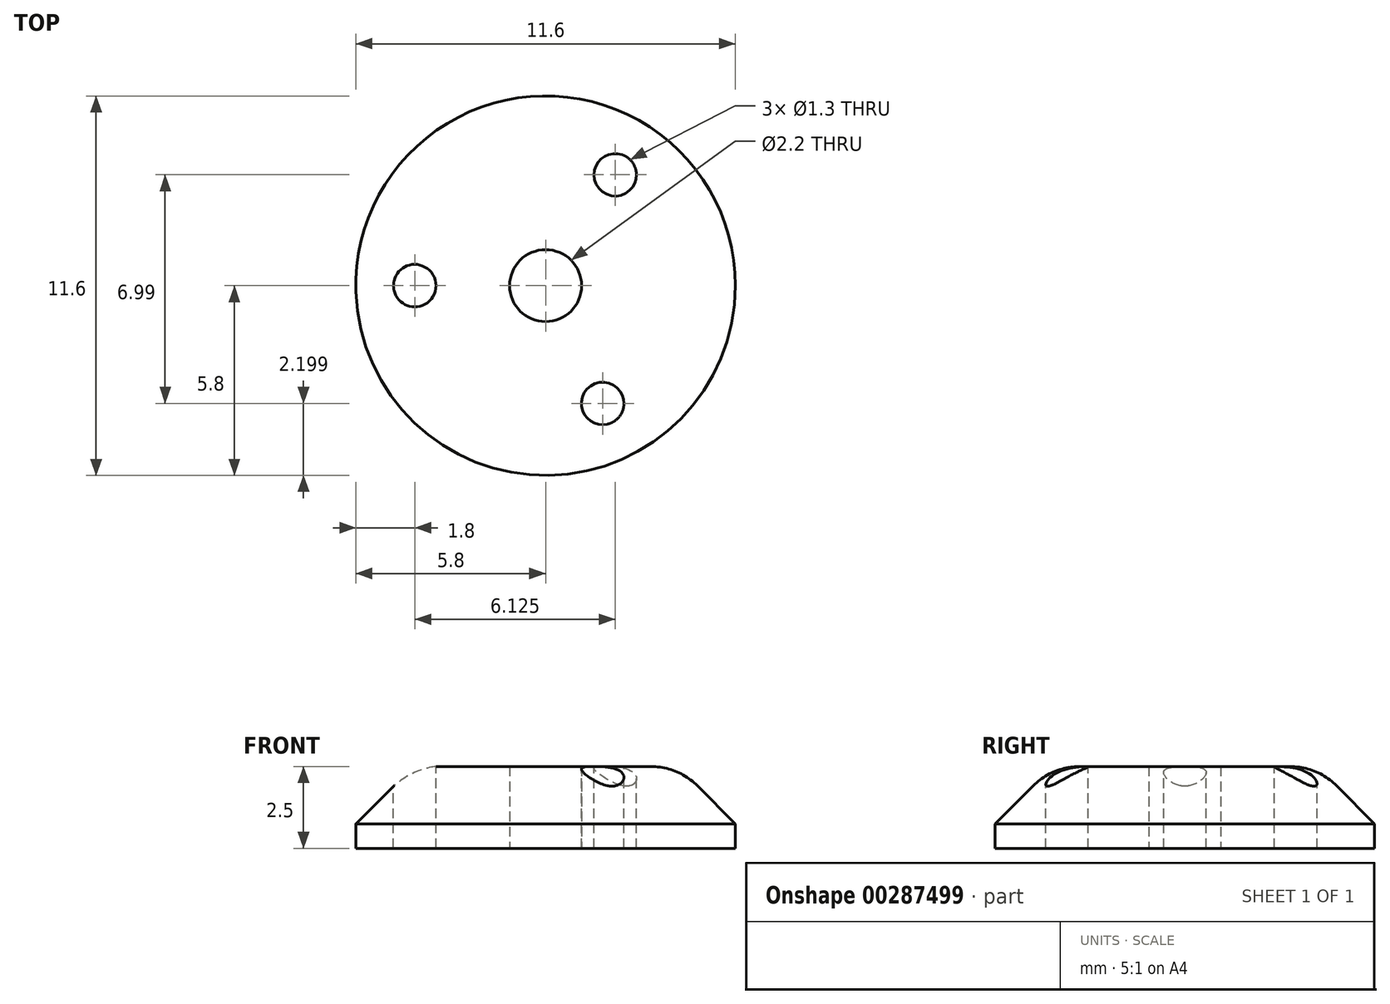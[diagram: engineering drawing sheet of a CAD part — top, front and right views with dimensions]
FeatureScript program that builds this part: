
annotation { "Feature Type Name" : "Feature", "Feature Type Description" : "" }
export const myFeature = defineFeature(function(context is Context, id is Id, definition is map)
    precondition{}
    {
        {
            var Q0;
            Q0=qCreatedBy(makeId("Top.planeOp"),FACE);
            var sketch = newSketch(context, id + "F0", { "sketchPlane" : qUnion([Q0])});
            skCircle(sketch, "E0", {"center": v(0, 0) * mm, "radius": 5.8 * mm});
            skCircle(sketch, "E1", {"center": v(0, 0) * mm, "radius": 1.1 * mm});
            skSolve(sketch);
        }
        {
            var Q0;
            Q0 = qSketchRegion(id + "F0", true);
            extrude(context, id + "F1", {"entities" : qUnion([Q0]), "depth" : 2.5 * mm});
        }
        {
            var Q0;
            Q0=makeQuery(id+"F1.opExtrude","CAP_FACE",FACE,{"disambiguationData":[OSD([sQuery(id+"F0.wireOp",EDGE,"E0"),sQuery(id+"F0.wireOp",EDGE,"E1")])],"isStart":false});
            var sketch = newSketch(context, id + "F2", { "sketchPlane" : qUnion([Q0])});
            skCircle(sketch, "E2", {"center": v(-4, 0) * mm, "radius": 0.65 * mm});
            skCircle(sketch, "E3", {"center": v(1.74, -3.6) * mm, "radius": 0.65 * mm});
            skCircle(sketch, "E4", {"center": v(2.13, 3.39) * mm, "radius": 0.65 * mm});
            skSolve(sketch);
        }
        {
            var Q0;
            Q0=makeQuery(id+"F2.imprint","IMPRINT",FACE,{"disambiguationData":[TD([[makeQuery(id+"F2.imprint","IMPRINT",EDGE,{"derivedFrom":sQuery(id+"F2.wireOp",EDGE,"E2")}),1.0]])]});
            var Q1;
            Q1=makeQuery(id+"F2.imprint","IMPRINT",FACE,{"disambiguationData":[TD([[makeQuery(id+"F2.imprint","IMPRINT",EDGE,{"derivedFrom":sQuery(id+"F2.wireOp",EDGE,"E4")}),1.0]])]});
            var Q2;
            Q2=makeQuery(id+"F2.imprint","IMPRINT",FACE,{"disambiguationData":[TD([[makeQuery(id+"F2.imprint","IMPRINT",EDGE,{"derivedFrom":sQuery(id+"F2.wireOp",EDGE,"E3")}),1.0]])]});
            extrude(context, id + "F3", {"entities" : qUnion([Q0, Q1, Q2]), "operationType" : NewBodyOperationType.REMOVE, "oppositeDirection" : true, "depth" : 25 * mm});
        }
        {
            var Q0;
            Q0=makeQuery(id+"F1.opExtrude","CAP_EDGE",EDGE,{"disambiguationData":[OSD([sQuery(id+"F0.wireOp",EDGE,"E0")])],"isStart":false});
            chamfer(context, id + "F4", {"entities" : qUnion([Q0]), "width" : 1.75 * mm, "tangentPropagation" : true});
        }
        {
            var Q0;
            {var subQ0=sQuery(id+"F0.wireOp",EDGE,"E0");Q0=makeQuery(id+"F4.opChamfer","BLEND_EDGE",EDGE,{"disambiguationData":[OD(1.0)],"blendedFrom":[makeQuery(id+"F1.opExtrude","CAP_EDGE",EDGE,{"disambiguationData":[OSD([subQ0])],"isStart":false}),makeQuery(id+"F1.opExtrude","CAP_FACE",FACE,{"disambiguationData":[OSD([subQ0,sQuery(id+"F0.wireOp",EDGE,"E1")])],"isStart":false})],"blendedInto":[makeQuery(id+"F1.opExtrude","CAP_FACE",FACE,{"disambiguationData":[OSD([subQ0,sQuery(id+"F0.wireOp",EDGE,"E1")])],"isStart":false})]});}
            var Q1;
            {var subQ0=sQuery(id+"F0.wireOp",EDGE,"E0");Q1=makeQuery(id+"F4.opChamfer","BLEND_EDGE",EDGE,{"disambiguationData":[OD(2.0)],"blendedFrom":[makeQuery(id+"F1.opExtrude","CAP_EDGE",EDGE,{"disambiguationData":[OSD([subQ0])],"isStart":false}),makeQuery(id+"F1.opExtrude","CAP_FACE",FACE,{"disambiguationData":[OSD([subQ0,sQuery(id+"F0.wireOp",EDGE,"E1")])],"isStart":false})],"blendedInto":[makeQuery(id+"F1.opExtrude","CAP_FACE",FACE,{"disambiguationData":[OSD([subQ0,sQuery(id+"F0.wireOp",EDGE,"E1")])],"isStart":false})]});}
            fillet(context, id + "F5", {"entities" : qUnion([Q0, Q1]), "radius" : 2 * mm, "tangentPropagation" : true, "allowEdgeOverflow" : false});
        }
    });
